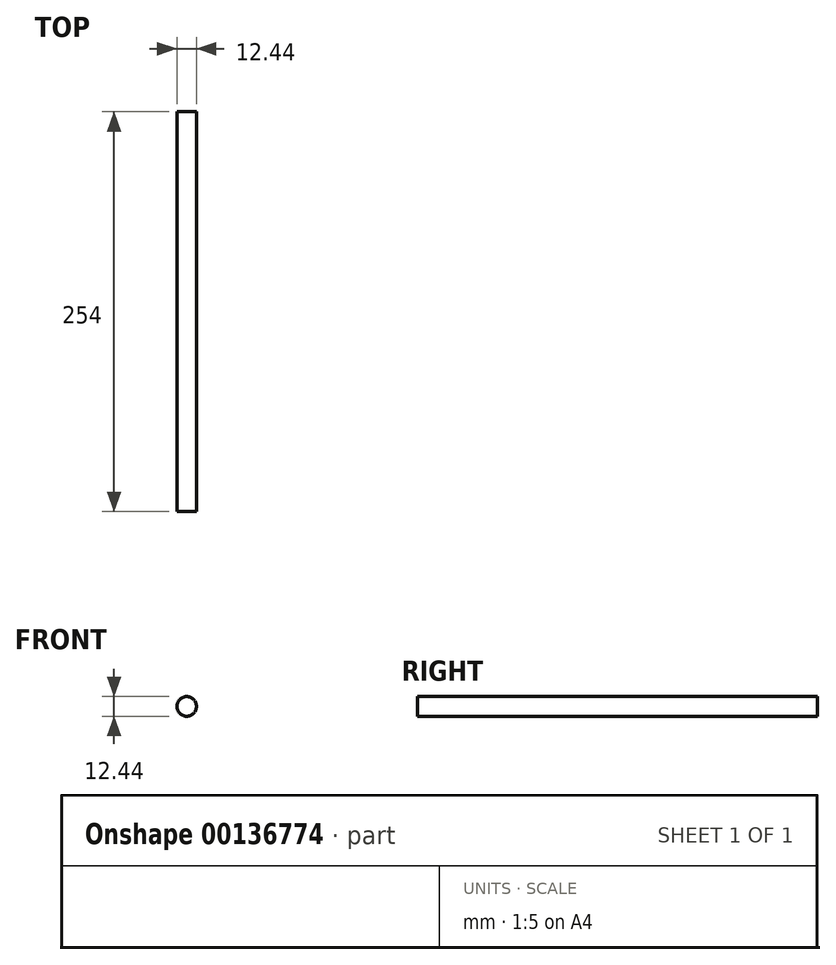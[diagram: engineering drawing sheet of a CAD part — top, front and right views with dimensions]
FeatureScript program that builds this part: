
annotation { "Feature Type Name" : "Feature", "Feature Type Description" : "" }
export const myFeature = defineFeature(function(context is Context, id is Id, definition is map)
    precondition{}
    {
        {
            var Q0;
            Q0=qCreatedBy(makeId("Front.planeOp"),FACE);
            var sketch = newSketch(context, id + "F0", { "sketchPlane" : qUnion([Q0])});
            skCircle(sketch, "E0", {"center": v(0, 0) * mm, "radius": 6.22 * mm});
            skSolve(sketch);
        }
        {
            var Q0;
            Q0 = qSketchRegion(id + "F0", true);
            extrude(context, id + "F1", {"entities" : qUnion([Q0]), "depth" : 254 * mm});
        }
    });
